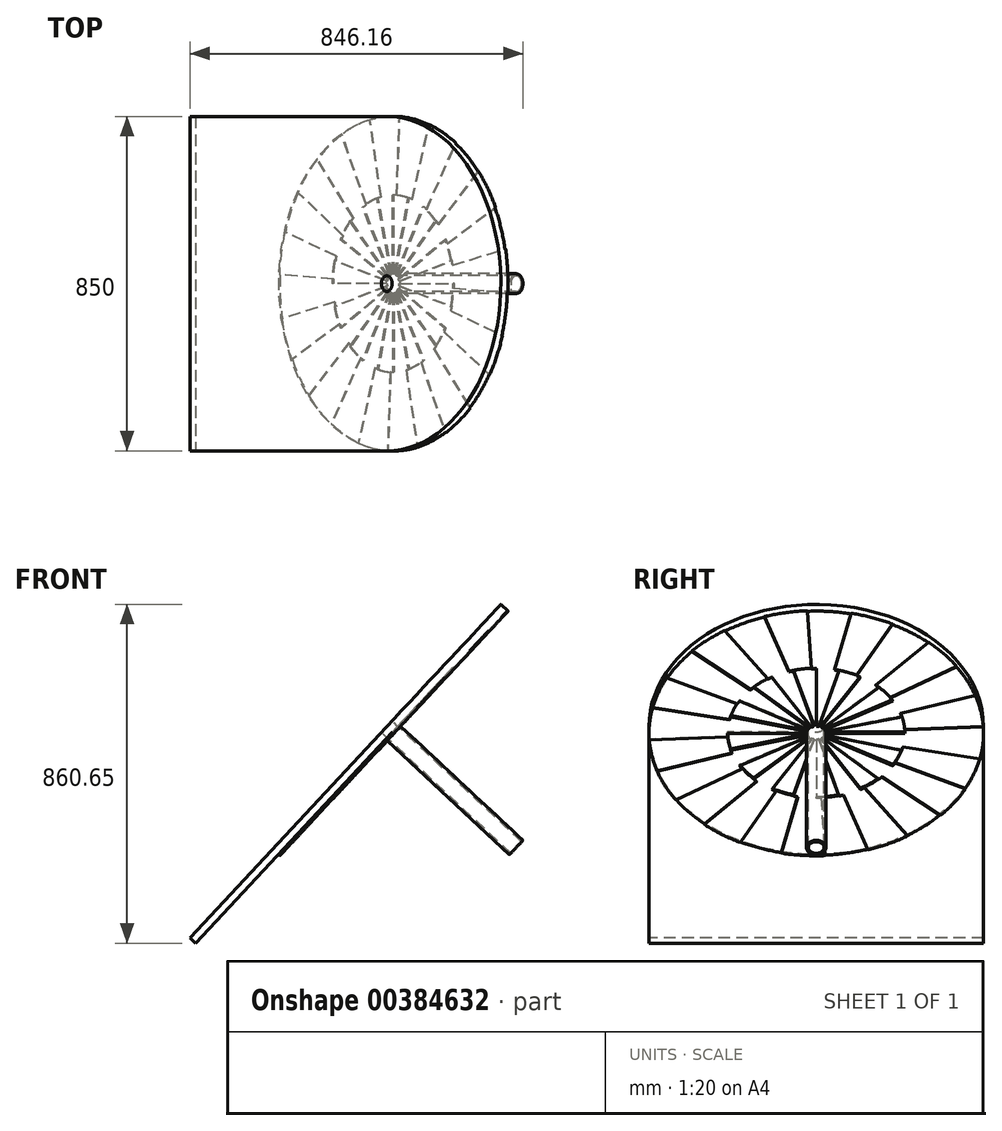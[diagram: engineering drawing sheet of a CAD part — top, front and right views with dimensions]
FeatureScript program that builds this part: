
annotation { "Feature Type Name" : "Feature", "Feature Type Description" : "" }
export const myFeature = defineFeature(function(context is Context, id is Id, definition is map)
    precondition{}
    {
        {
            var Q0;
            Q0=qCreatedBy(makeId("Front.planeOp"),FACE);
            var sketch = newSketch(context, id + "F0", { "sketchPlane" : qUnion([Q0])});
            skLineSegment(sketch, "E0", {"start": v(0, 0) * mm, "end": v(1000, 0) * mm, "construction": true});
            skLineSegment(sketch, "E1", {"start": v(1000, 0) * mm, "end": v(0, 932.52) * mm, "construction": true});
            skSolve(sketch);
        }
        {
            var Q0;
            Q0=sQuery(id+"F0.wireOp",EDGE,"E1");
            cPlane(context, id + "F1", {"entities" : qUnion([Q0]), "cplaneType" : CPlaneType.MID_PLANE, "offset" : 25 * mm, "width" : 150 * mm, "height" : 150 * mm});
        }
        {
            var Q0;
            Q0=qCreatedBy(id+"F1.planeOp",FACE);
            var sketch = newSketch(context, id + "F2", { "sketchPlane" : qUnion([Q0])});
            skPoint(sketch, "E2.0", {"position": v(0, 682) * mm});
            skCircle(sketch, "E3", {"center": v(0, 682) * mm, "radius": 25 * mm});
            skCircle(sketch, "E4.0", {"center": v(0, 682) * mm, "radius": 20 * mm});
            skCircle(sketch, "E5.0", {"center": v(0, 682) * mm, "radius": 225 * mm});
            skCircle(sketch, "E6.0", {"center": v(0, 682) * mm, "radius": 425 * mm});
            skLineSegment(sketch, "E7", {"start": v(-425, -51.14) * mm, "end": v(425, -51.14) * mm});
            skLineSegment(sketch, "E8", {"start": v(425, -51.14) * mm, "end": v(425, 682) * mm});
            skLineSegment(sketch, "E9", {"start": v(-425, 682) * mm, "end": v(-425, -51.14) * mm});
            skLineSegment(sketch, "E10", {"start": v(0, 707) * mm, "end": v(0, 907) * mm});
            skLineSegment(sketch, "E11.1.0", {"start": v(-6.47, 706.15) * mm, "end": v(-58.23, 899.33) * mm});
            skLineSegment(sketch, "E11.2.0", {"start": v(-12.5, 703.65) * mm, "end": v(-112.5, 876.85) * mm});
            skLineSegment(sketch, "E11.3.0", {"start": v(-17.68, 699.68) * mm, "end": v(-159.1, 841.1) * mm});
            skLineSegment(sketch, "E11.4.0", {"start": v(-21.65, 694.5) * mm, "end": v(-194.86, 794.5) * mm});
            skLineSegment(sketch, "E11.5.0", {"start": v(-24.15, 688.47) * mm, "end": v(-217.33, 740.23) * mm});
            skLineSegment(sketch, "E11.6.0", {"start": v(-25, 682) * mm, "end": v(-225, 682) * mm});
            skLineSegment(sketch, "E11.7.0", {"start": v(-24.15, 675.53) * mm, "end": v(-217.33, 623.76) * mm});
            skLineSegment(sketch, "E11.8.0", {"start": v(-21.65, 669.5) * mm, "end": v(-194.86, 569.5) * mm});
            skLineSegment(sketch, "E11.9.0", {"start": v(-17.68, 664.32) * mm, "end": v(-159.1, 522.9) * mm});
            skLineSegment(sketch, "E11.10.0", {"start": v(-12.5, 660.35) * mm, "end": v(-112.5, 487.14) * mm});
            skLineSegment(sketch, "E11.11.0", {"start": v(-6.47, 657.85) * mm, "end": v(-58.23, 464.67) * mm});
            skLineSegment(sketch, "E11.12.0", {"start": v(0, 657) * mm, "end": v(0, 457) * mm});
            skLineSegment(sketch, "E11.13.0", {"start": v(6.47, 657.85) * mm, "end": v(58.23, 464.67) * mm});
            skLineSegment(sketch, "E11.14.0", {"start": v(12.5, 660.35) * mm, "end": v(112.5, 487.14) * mm});
            skLineSegment(sketch, "E11.15.0", {"start": v(17.68, 664.32) * mm, "end": v(159.1, 522.9) * mm});
            skLineSegment(sketch, "E11.16.0", {"start": v(21.65, 669.5) * mm, "end": v(194.86, 569.5) * mm});
            skLineSegment(sketch, "E11.17.0", {"start": v(24.15, 675.53) * mm, "end": v(217.33, 623.76) * mm});
            skLineSegment(sketch, "E11.18.0", {"start": v(25, 682) * mm, "end": v(225, 682) * mm});
            skLineSegment(sketch, "E11.19.0", {"start": v(24.15, 688.47) * mm, "end": v(217.33, 740.23) * mm});
            skLineSegment(sketch, "E11.20.0", {"start": v(21.65, 694.5) * mm, "end": v(194.86, 794.5) * mm});
            skLineSegment(sketch, "E11.21.0", {"start": v(17.68, 699.68) * mm, "end": v(159.1, 841.1) * mm});
            skLineSegment(sketch, "E11.22.0", {"start": v(12.5, 703.65) * mm, "end": v(112.5, 876.85) * mm});
            skLineSegment(sketch, "E11.23.0", {"start": v(6.47, 706.15) * mm, "end": v(58.23, 899.33) * mm});
            skLineSegment(sketch, "E12", {"start": v(0, 907) * mm, "end": v(0, 1107) * mm, "construction": true});
            skLineSegment(sketch, "E13", {"start": v(11.78, 906.7) * mm, "end": v(22.24, 1106.42) * mm});
            skLineSegment(sketch, "E14.1.0", {"start": v(-46.78, 902.08) * mm, "end": v(-88.36, 1097.71) * mm});
            skLineSegment(sketch, "E14.2.0", {"start": v(-102.15, 882.47) * mm, "end": v(-192.95, 1060.68) * mm});
            skLineSegment(sketch, "E14.3.0", {"start": v(-150.55, 849.2) * mm, "end": v(-284.38, 997.83) * mm});
            skLineSegment(sketch, "E14.4.0", {"start": v(-188.7, 804.54) * mm, "end": v(-356.43, 913.47) * mm});
            skLineSegment(sketch, "E14.5.0", {"start": v(-213.99, 751.53) * mm, "end": v(-404.2, 813.33) * mm});
            skLineSegment(sketch, "E14.6.0", {"start": v(-224.7, 693.77) * mm, "end": v(-424.42, 704.24) * mm});
            skLineSegment(sketch, "E14.7.0", {"start": v(-220.08, 635.22) * mm, "end": v(-415.71, 593.64) * mm});
            skLineSegment(sketch, "E14.8.0", {"start": v(-200.48, 579.85) * mm, "end": v(-378.68, 489.05) * mm});
            skLineSegment(sketch, "E14.9.0", {"start": v(-167.2, 531.44) * mm, "end": v(-315.84, 397.62) * mm});
            skLineSegment(sketch, "E14.10.0", {"start": v(-122.54, 493.3) * mm, "end": v(-231.47, 325.56) * mm});
            skLineSegment(sketch, "E14.11.0", {"start": v(-69.53, 468.01) * mm, "end": v(-131.33, 277.8) * mm});
            skLineSegment(sketch, "E14.12.0", {"start": v(-11.78, 457.3) * mm, "end": v(-22.24, 257.58) * mm});
            skLineSegment(sketch, "E14.13.0", {"start": v(46.78, 461.92) * mm, "end": v(88.36, 266.29) * mm});
            skLineSegment(sketch, "E14.14.0", {"start": v(102.15, 481.52) * mm, "end": v(192.95, 303.32) * mm});
            skLineSegment(sketch, "E14.15.0", {"start": v(150.55, 514.8) * mm, "end": v(284.38, 366.16) * mm});
            skLineSegment(sketch, "E14.16.0", {"start": v(188.7, 559.45) * mm, "end": v(356.43, 450.53) * mm});
            skLineSegment(sketch, "E14.17.0", {"start": v(213.99, 612.47) * mm, "end": v(404.2, 550.67) * mm});
            skLineSegment(sketch, "E14.18.0", {"start": v(224.7, 670.22) * mm, "end": v(424.42, 659.76) * mm});
            skLineSegment(sketch, "E14.19.0", {"start": v(220.08, 728.78) * mm, "end": v(415.71, 770.36) * mm});
            skLineSegment(sketch, "E14.20.0", {"start": v(200.48, 784.15) * mm, "end": v(378.68, 874.94) * mm});
            skLineSegment(sketch, "E14.21.0", {"start": v(167.2, 832.55) * mm, "end": v(315.84, 966.38) * mm});
            skLineSegment(sketch, "E14.22.0", {"start": v(122.54, 870.7) * mm, "end": v(231.47, 1038.43) * mm});
            skLineSegment(sketch, "E14.23.0", {"start": v(69.53, 895.99) * mm, "end": v(131.33, 1086.2) * mm});
            skSolve(sketch);
        }
        {
            var Q0;
            Q0=qCreatedBy(makeId("Front.planeOp"),FACE);
            var sketch = newSketch(context, id + "F3", { "sketchPlane" : qUnion([Q0])});
            skLineSegment(sketch, "E15.0", {"start": v(500, 466.26) * mm, "end": v(166.68, 777.08) * mm});
            skLineSegment(sketch, "E16.0", {"start": v(500, 466.26) * mm, "end": v(0, -69.93) * mm});
            skLineSegment(sketch, "E17.0", {"start": v(210.15, 155.43) * mm, "end": v(789.85, 777.08) * mm});
            skLineSegment(sketch, "E18", {"start": v(789.85, 777.08) * mm, "end": v(0, 777.08) * mm});
            skLineSegment(sketch, "E19", {"start": v(0, 777.08) * mm, "end": v(0, -69.93) * mm});
            skLineSegment(sketch, "E20.0", {"start": v(503.4, 469.91) * mm, "end": v(174.01, 777.08) * mm});
            skPoint(sketch, "E21.orphan", {"position": v(1000, 0) * mm});
            skLineSegment(sketch, "E22.MirrorCS", {"start": v(496.6, 462.6) * mm, "end": v(159.35, 777.08) * mm});
            skPoint(sketch, "E23.orphan", {"position": v(-3.4, 928.86) * mm});
            skPoint(sketch, "E24.orphan", {"position": v(0, 932.52) * mm});
            skPoint(sketch, "E25.orphan", {"position": v(3.4, 936.17) * mm});
            skLineSegment(sketch, "E26", {"start": v(789.85, 777.08) * mm, "end": v(-181.34, -1891.25) * mm, "construction": true});
            skSolve(sketch);
        }
        {
            var Q0;
            Q0=makeQuery(id+"F2.imprint","IMPRINT",FACE,{"disambiguationData":[TD([[makeQuery(id+"F2.imprint","IMPRINT",EDGE,{"derivedFrom":sQuery(id+"F2.wireOp",EDGE,"E7")}),1.0]])]});
            var Q1;
            {var subQ0=sQuery(id+"F2.wireOp",EDGE,"E10");Q1=makeQuery(id+"F2.imprint","IMPRINT",FACE,{"disambiguationData":[TD([[makeQuery(id+"F2.imprint","IMPRINT",EDGE,{"derivedFrom":subQ0}),-1.0]])]});}
            var Q2;
            {var subQ3=sQuery(id+"F2.wireOp",EDGE,"E11.21.0");Q2=makeQuery(id+"F2.imprint","IMPRINT",FACE,{"disambiguationData":[TD([[makeQuery(id+"F2.imprint","IMPRINT",EDGE,{"derivedFrom":subQ3}),1.0]])]});}
            var Q3;
            {var subQ3=sQuery(id+"F2.wireOp",EDGE,"E11.19.0");Q3=makeQuery(id+"F2.imprint","IMPRINT",FACE,{"disambiguationData":[TD([[makeQuery(id+"F2.imprint","IMPRINT",EDGE,{"derivedFrom":subQ3}),1.0]])]});}
            var Q4;
            {var subQ0=sQuery(id+"F2.wireOp",EDGE,"E11.17.0");Q4=makeQuery(id+"F2.imprint","IMPRINT",FACE,{"disambiguationData":[TD([[makeQuery(id+"F2.imprint","IMPRINT",EDGE,{"derivedFrom":subQ0}),1.0]])]});}
            var Q5;
            {var subQ3=sQuery(id+"F2.wireOp",EDGE,"E11.15.0");Q5=makeQuery(id+"F2.imprint","IMPRINT",FACE,{"disambiguationData":[TD([[makeQuery(id+"F2.imprint","IMPRINT",EDGE,{"derivedFrom":subQ3}),1.0]])]});}
            var Q6;
            {var subQ0=sQuery(id+"F2.wireOp",EDGE,"E11.13.0");Q6=makeQuery(id+"F2.imprint","IMPRINT",FACE,{"disambiguationData":[TD([[makeQuery(id+"F2.imprint","IMPRINT",EDGE,{"derivedFrom":subQ0}),1.0]])]});}
            var Q7;
            {var subQ0=sQuery(id+"F2.wireOp",EDGE,"E11.11.0");Q7=makeQuery(id+"F2.imprint","IMPRINT",FACE,{"disambiguationData":[TD([[makeQuery(id+"F2.imprint","IMPRINT",EDGE,{"derivedFrom":subQ0}),1.0]])]});}
            var Q8;
            {var subQ0=sQuery(id+"F2.wireOp",EDGE,"E11.9.0");Q8=makeQuery(id+"F2.imprint","IMPRINT",FACE,{"disambiguationData":[TD([[makeQuery(id+"F2.imprint","IMPRINT",EDGE,{"derivedFrom":subQ0}),1.0]])]});}
            var Q9;
            {var subQ0=sQuery(id+"F2.wireOp",EDGE,"E11.7.0");Q9=makeQuery(id+"F2.imprint","IMPRINT",FACE,{"disambiguationData":[TD([[makeQuery(id+"F2.imprint","IMPRINT",EDGE,{"derivedFrom":subQ0}),1.0]])]});}
            var Q10;
            {var subQ3=sQuery(id+"F2.wireOp",EDGE,"E11.5.0");Q10=makeQuery(id+"F2.imprint","IMPRINT",FACE,{"disambiguationData":[TD([[makeQuery(id+"F2.imprint","IMPRINT",EDGE,{"derivedFrom":subQ3}),1.0]])]});}
            var Q11;
            {var subQ0=sQuery(id+"F2.wireOp",EDGE,"E11.3.0");Q11=makeQuery(id+"F2.imprint","IMPRINT",FACE,{"disambiguationData":[TD([[makeQuery(id+"F2.imprint","IMPRINT",EDGE,{"derivedFrom":subQ0}),1.0]])]});}
            var Q12;
            {var subQ0=sQuery(id+"F2.wireOp",EDGE,"E11.1.0");Q12=makeQuery(id+"F2.imprint","IMPRINT",FACE,{"disambiguationData":[TD([[makeQuery(id+"F2.imprint","IMPRINT",EDGE,{"derivedFrom":subQ0}),1.0]])]});}
            extrude(context, id + "F4", {"entities" : qUnion([Q0, Q1, Q2, Q3, Q4, Q5, Q6, Q7, Q8, Q9, Q10, Q11, Q12]), "oppositeDirection" : true, "depth" : 20 * mm});
        }
        {
            var Q0;
            {var subQ3=sQuery(id+"F2.wireOp",EDGE,"E11.20.0");Q0=makeQuery(id+"F2.imprint","IMPRINT",FACE,{"disambiguationData":[TD([[makeQuery(id+"F2.imprint","IMPRINT",EDGE,{"derivedFrom":subQ3}),1.0]])]});}
            var Q1;
            {var subQ0=sQuery(id+"F2.wireOp",EDGE,"E11.22.0");Q1=makeQuery(id+"F2.imprint","IMPRINT",FACE,{"disambiguationData":[TD([[makeQuery(id+"F2.imprint","IMPRINT",EDGE,{"derivedFrom":subQ0}),1.0]])]});}
            var Q2;
            {var subQ3=sQuery(id+"F2.wireOp",EDGE,"E10");Q2=makeQuery(id+"F2.imprint","IMPRINT",FACE,{"disambiguationData":[TD([[makeQuery(id+"F2.imprint","IMPRINT",EDGE,{"derivedFrom":subQ3}),1.0]])]});}
            var Q3;
            {var subQ0=sQuery(id+"F2.wireOp",EDGE,"E11.2.0");Q3=makeQuery(id+"F2.imprint","IMPRINT",FACE,{"disambiguationData":[TD([[makeQuery(id+"F2.imprint","IMPRINT",EDGE,{"derivedFrom":subQ0}),1.0]])]});}
            var Q4;
            {var subQ0=sQuery(id+"F2.wireOp",EDGE,"E11.4.0");Q4=makeQuery(id+"F2.imprint","IMPRINT",FACE,{"disambiguationData":[TD([[makeQuery(id+"F2.imprint","IMPRINT",EDGE,{"derivedFrom":subQ0}),1.0]])]});}
            var Q5;
            {var subQ0=sQuery(id+"F2.wireOp",EDGE,"E11.6.0");Q5=makeQuery(id+"F2.imprint","IMPRINT",FACE,{"disambiguationData":[TD([[makeQuery(id+"F2.imprint","IMPRINT",EDGE,{"derivedFrom":subQ0}),1.0]])]});}
            var Q6;
            {var subQ0=sQuery(id+"F2.wireOp",EDGE,"E11.8.0");Q6=makeQuery(id+"F2.imprint","IMPRINT",FACE,{"disambiguationData":[TD([[makeQuery(id+"F2.imprint","IMPRINT",EDGE,{"derivedFrom":subQ0}),1.0]])]});}
            var Q7;
            {var subQ3=sQuery(id+"F2.wireOp",EDGE,"E11.10.0");Q7=makeQuery(id+"F2.imprint","IMPRINT",FACE,{"disambiguationData":[TD([[makeQuery(id+"F2.imprint","IMPRINT",EDGE,{"derivedFrom":subQ3}),1.0]])]});}
            var Q8;
            {var subQ0=sQuery(id+"F2.wireOp",EDGE,"E11.12.0");Q8=makeQuery(id+"F2.imprint","IMPRINT",FACE,{"disambiguationData":[TD([[makeQuery(id+"F2.imprint","IMPRINT",EDGE,{"derivedFrom":subQ0}),1.0]])]});}
            var Q9;
            {var subQ0=sQuery(id+"F2.wireOp",EDGE,"E11.14.0");Q9=makeQuery(id+"F2.imprint","IMPRINT",FACE,{"disambiguationData":[TD([[makeQuery(id+"F2.imprint","IMPRINT",EDGE,{"derivedFrom":subQ0}),1.0]])]});}
            var Q10;
            {var subQ0=sQuery(id+"F2.wireOp",EDGE,"E11.16.0");Q10=makeQuery(id+"F2.imprint","IMPRINT",FACE,{"disambiguationData":[TD([[makeQuery(id+"F2.imprint","IMPRINT",EDGE,{"derivedFrom":subQ0}),1.0]])]});}
            var Q11;
            {var subQ3=sQuery(id+"F2.wireOp",EDGE,"E11.18.0");Q11=makeQuery(id+"F2.imprint","IMPRINT",FACE,{"disambiguationData":[TD([[makeQuery(id+"F2.imprint","IMPRINT",EDGE,{"derivedFrom":subQ3}),1.0]])]});}
            extrude(context, id + "F5", {"entities" : qUnion([Q0, Q1, Q2, Q3, Q4, Q5, Q6, Q7, Q8, Q9, Q10, Q11]), "oppositeDirection" : true, "depth" : 25 * mm});
        }
        {
            var Q0;
            {var subQ0=sQuery(id+"F2.wireOp",EDGE,"E14.13.0");Q0=makeQuery(id+"F2.imprint","IMPRINT",FACE,{"disambiguationData":[TD([[makeQuery(id+"F2.imprint","IMPRINT",EDGE,{"derivedFrom":subQ0}),1.0]])]});}
            var Q1;
            {var subQ0=sQuery(id+"F2.wireOp",EDGE,"E14.15.0");Q1=makeQuery(id+"F2.imprint","IMPRINT",FACE,{"disambiguationData":[TD([[makeQuery(id+"F2.imprint","IMPRINT",EDGE,{"derivedFrom":subQ0}),1.0]])]});}
            var Q2;
            {var subQ0=sQuery(id+"F2.wireOp",EDGE,"E14.17.0");Q2=makeQuery(id+"F2.imprint","IMPRINT",FACE,{"disambiguationData":[TD([[makeQuery(id+"F2.imprint","IMPRINT",EDGE,{"derivedFrom":subQ0}),1.0]])]});}
            var Q3;
            {var subQ0=sQuery(id+"F2.wireOp",EDGE,"E14.19.0");Q3=makeQuery(id+"F2.imprint","IMPRINT",FACE,{"disambiguationData":[TD([[makeQuery(id+"F2.imprint","IMPRINT",EDGE,{"derivedFrom":subQ0}),1.0]])]});}
            var Q4;
            {var subQ0=sQuery(id+"F2.wireOp",EDGE,"E14.21.0");Q4=makeQuery(id+"F2.imprint","IMPRINT",FACE,{"disambiguationData":[TD([[makeQuery(id+"F2.imprint","IMPRINT",EDGE,{"derivedFrom":subQ0}),1.0]])]});}
            var Q5;
            {var subQ0=sQuery(id+"F2.wireOp",EDGE,"E13");Q5=makeQuery(id+"F2.imprint","IMPRINT",FACE,{"disambiguationData":[TD([[makeQuery(id+"F2.imprint","IMPRINT",EDGE,{"derivedFrom":subQ0}),-1.0]])]});}
            var Q6;
            {var subQ0=sQuery(id+"F2.wireOp",EDGE,"E14.1.0");Q6=makeQuery(id+"F2.imprint","IMPRINT",FACE,{"disambiguationData":[TD([[makeQuery(id+"F2.imprint","IMPRINT",EDGE,{"derivedFrom":subQ0}),1.0]])]});}
            var Q7;
            {var subQ0=sQuery(id+"F2.wireOp",EDGE,"E14.3.0");Q7=makeQuery(id+"F2.imprint","IMPRINT",FACE,{"disambiguationData":[TD([[makeQuery(id+"F2.imprint","IMPRINT",EDGE,{"derivedFrom":subQ0}),1.0]])]});}
            var Q8;
            {var subQ0=sQuery(id+"F2.wireOp",EDGE,"E14.5.0");Q8=makeQuery(id+"F2.imprint","IMPRINT",FACE,{"disambiguationData":[TD([[makeQuery(id+"F2.imprint","IMPRINT",EDGE,{"derivedFrom":subQ0}),1.0]])]});}
            var Q9;
            {var subQ0=sQuery(id+"F2.wireOp",EDGE,"E14.7.0");Q9=makeQuery(id+"F2.imprint","IMPRINT",FACE,{"disambiguationData":[TD([[makeQuery(id+"F2.imprint","IMPRINT",EDGE,{"derivedFrom":subQ0}),1.0]])]});}
            var Q10;
            {var subQ0=sQuery(id+"F2.wireOp",EDGE,"E14.9.0");Q10=makeQuery(id+"F2.imprint","IMPRINT",FACE,{"disambiguationData":[TD([[makeQuery(id+"F2.imprint","IMPRINT",EDGE,{"derivedFrom":subQ0}),1.0]])]});}
            var Q11;
            {var subQ0=sQuery(id+"F2.wireOp",EDGE,"E14.11.0");Q11=makeQuery(id+"F2.imprint","IMPRINT",FACE,{"disambiguationData":[TD([[makeQuery(id+"F2.imprint","IMPRINT",EDGE,{"derivedFrom":subQ0}),1.0]])]});}
            extrude(context, id + "F6", {"entities" : qUnion([Q0, Q1, Q2, Q3, Q4, Q5, Q6, Q7, Q8, Q9, Q10, Q11]), "operationType" : NewBodyOperationType.ADD, "oppositeDirection" : true, "depth" : 23 * mm});
        }
        {
            var Q0;
            {var subQ0=sQuery(id+"F2.wireOp",EDGE,"E14.14.0");Q0=makeQuery(id+"F2.imprint","IMPRINT",FACE,{"disambiguationData":[TD([[makeQuery(id+"F2.imprint","IMPRINT",EDGE,{"derivedFrom":subQ0}),1.0]])]});}
            var Q1;
            {var subQ0=sQuery(id+"F2.wireOp",EDGE,"E14.16.0");Q1=makeQuery(id+"F2.imprint","IMPRINT",FACE,{"disambiguationData":[TD([[makeQuery(id+"F2.imprint","IMPRINT",EDGE,{"derivedFrom":subQ0}),1.0]])]});}
            var Q2;
            {var subQ2=sQuery(id+"F2.wireOp",EDGE,"E14.18.0");Q2=makeQuery(id+"F2.imprint","IMPRINT",FACE,{"disambiguationData":[TD([[makeQuery(id+"F2.imprint","IMPRINT",EDGE,{"derivedFrom":subQ2}),1.0]])]});}
            var Q3;
            {var subQ0=sQuery(id+"F2.wireOp",EDGE,"E14.20.0");Q3=makeQuery(id+"F2.imprint","IMPRINT",FACE,{"disambiguationData":[TD([[makeQuery(id+"F2.imprint","IMPRINT",EDGE,{"derivedFrom":subQ0}),1.0]])]});}
            var Q4;
            {var subQ0=sQuery(id+"F2.wireOp",EDGE,"E14.22.0");Q4=makeQuery(id+"F2.imprint","IMPRINT",FACE,{"disambiguationData":[TD([[makeQuery(id+"F2.imprint","IMPRINT",EDGE,{"derivedFrom":subQ0}),1.0]])]});}
            var Q5;
            {var subQ0=sQuery(id+"F2.wireOp",EDGE,"E13");Q5=makeQuery(id+"F2.imprint","IMPRINT",FACE,{"disambiguationData":[TD([[makeQuery(id+"F2.imprint","IMPRINT",EDGE,{"derivedFrom":subQ0}),1.0]])]});}
            var Q6;
            {var subQ0=sQuery(id+"F2.wireOp",EDGE,"E14.2.0");Q6=makeQuery(id+"F2.imprint","IMPRINT",FACE,{"disambiguationData":[TD([[makeQuery(id+"F2.imprint","IMPRINT",EDGE,{"derivedFrom":subQ0}),1.0]])]});}
            var Q7;
            {var subQ0=sQuery(id+"F2.wireOp",EDGE,"E14.4.0");Q7=makeQuery(id+"F2.imprint","IMPRINT",FACE,{"disambiguationData":[TD([[makeQuery(id+"F2.imprint","IMPRINT",EDGE,{"derivedFrom":subQ0}),1.0]])]});}
            var Q8;
            {var subQ3=sQuery(id+"F2.wireOp",EDGE,"E14.6.0");Q8=makeQuery(id+"F2.imprint","IMPRINT",FACE,{"disambiguationData":[TD([[makeQuery(id+"F2.imprint","IMPRINT",EDGE,{"derivedFrom":subQ3}),1.0]])]});}
            var Q9;
            {var subQ0=sQuery(id+"F2.wireOp",EDGE,"E14.8.0");Q9=makeQuery(id+"F2.imprint","IMPRINT",FACE,{"disambiguationData":[TD([[makeQuery(id+"F2.imprint","IMPRINT",EDGE,{"derivedFrom":subQ0}),1.0]])]});}
            var Q10;
            {var subQ0=sQuery(id+"F2.wireOp",EDGE,"E14.10.0");Q10=makeQuery(id+"F2.imprint","IMPRINT",FACE,{"disambiguationData":[TD([[makeQuery(id+"F2.imprint","IMPRINT",EDGE,{"derivedFrom":subQ0}),1.0]])]});}
            var Q11;
            {var subQ0=sQuery(id+"F2.wireOp",EDGE,"E14.12.0");Q11=makeQuery(id+"F2.imprint","IMPRINT",FACE,{"disambiguationData":[TD([[makeQuery(id+"F2.imprint","IMPRINT",EDGE,{"derivedFrom":subQ0}),1.0]])]});}
            extrude(context, id + "F7", {"entities" : qUnion([Q0, Q1, Q2, Q3, Q4, Q5, Q6, Q7, Q8, Q9, Q10, Q11]), "operationType" : NewBodyOperationType.ADD, "oppositeDirection" : true, "depth" : 25 * mm});
        }
        {
            var Q0;
            Q0=makeQuery(id+"F2.imprint","IMPRINT",FACE,{"disambiguationData":[TD([[makeQuery(id+"F2.imprint","IMPRINT",EDGE,{"derivedFrom":sQuery(id+"F2.wireOp",EDGE,"E4.0")}),-1.0]])]});
            extrude(context, id + "F8", {"entities" : qUnion([Q0]), "operationType" : NewBodyOperationType.ADD, "oppositeDirection" : true, "depth" : 450 * mm});
        }
    });
